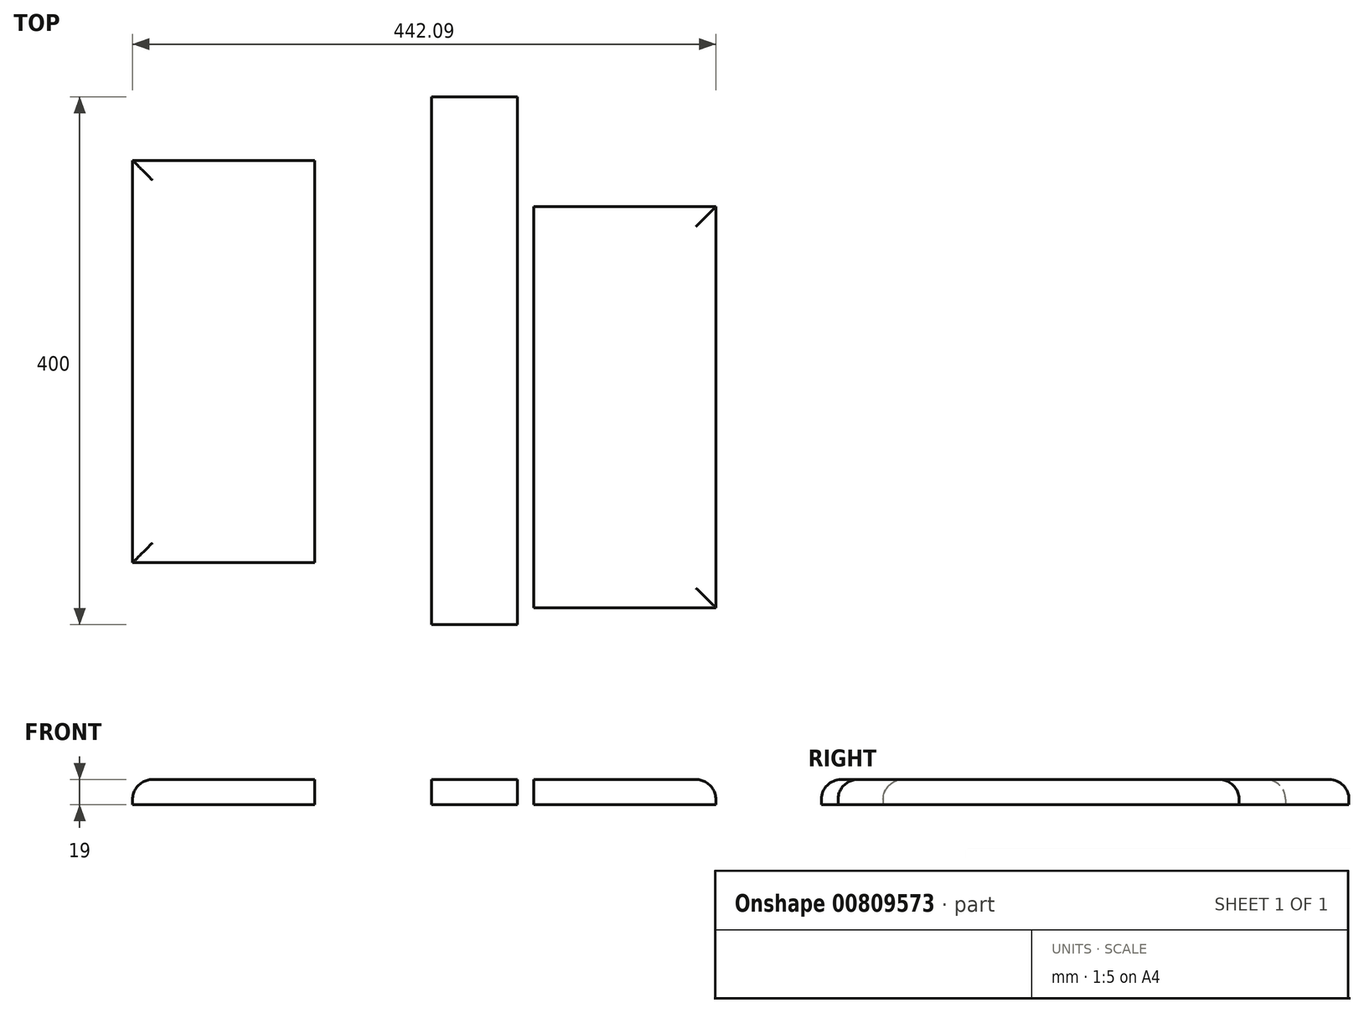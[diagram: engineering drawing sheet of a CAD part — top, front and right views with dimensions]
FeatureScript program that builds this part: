
annotation { "Feature Type Name" : "Feature", "Feature Type Description" : "" }
export const myFeature = defineFeature(function(context is Context, id is Id, definition is map)
    precondition{}
    {
        {
            var Q0;
            Q0=qCreatedBy(makeId("Top.planeOp"),FACE);
            var sketch = newSketch(context, id + "F0", { "sketchPlane" : qUnion([Q0])});
            skLineSegment(sketch, "E0.bottom", {"start": v(-51.89, 169.58) * mm, "end": v(-116.89, 169.58) * mm});
            skLineSegment(sketch, "E0.top", {"start": v(-51.89, -230.42) * mm, "end": v(-116.89, -230.42) * mm});
            skLineSegment(sketch, "E0.left", {"start": v(-51.89, 169.58) * mm, "end": v(-51.89, -230.42) * mm});
            skLineSegment(sketch, "E0.right", {"start": v(-116.89, 169.58) * mm, "end": v(-116.89, -230.42) * mm});
            skSolve(sketch);
        }
        {
            var Q0;
            Q0=makeQuery(id+"F0.imprint","IMPRINT",FACE,{"disambiguationData":[TD([[makeQuery(id+"F0.imprint","IMPRINT",EDGE,{"derivedFrom":sQuery(id+"F0.wireOp",EDGE,"E0.bottom")}),1.0]])]});
            extrude(context, id + "F1", {"entities" : qUnion([Q0]), "depth" : 19 * mm, "offsetDistance" : 25 * mm});
        }
        {
            var Q0;
            Q0=qCreatedBy(makeId("Top.planeOp"),FACE);
            var sketch = newSketch(context, id + "F2", { "sketchPlane" : qUnion([Q0])});
            skLineSegment(sketch, "E1.bottom", {"start": v(-39.45, 86.28) * mm, "end": v(98.55, 86.28) * mm});
            skLineSegment(sketch, "E1.top", {"start": v(-39.45, -217.74) * mm, "end": v(98.55, -217.74) * mm});
            skLineSegment(sketch, "E1.left", {"start": v(-39.45, 86.28) * mm, "end": v(-39.45, -217.74) * mm});
            skLineSegment(sketch, "E1.right", {"start": v(98.55, 86.28) * mm, "end": v(98.55, -217.74) * mm});
            skSolve(sketch);
        }
        {
            var Q0;
            Q0=makeQuery(id+"F2.imprint","IMPRINT",FACE,{"disambiguationData":[TD([[makeQuery(id+"F2.imprint","IMPRINT",EDGE,{"derivedFrom":sQuery(id+"F2.wireOp",EDGE,"E1.bottom")}),-1.0]])]});
            extrude(context, id + "F3", {"entities" : qUnion([Q0]), "depth" : 19 * mm, "offsetDistance" : 25 * mm});
        }
        {
            var Q0;
            Q0=qCreatedBy(makeId("Top.planeOp"),FACE);
            var sketch = newSketch(context, id + "F4", { "sketchPlane" : qUnion([Q0])});
            skLineSegment(sketch, "E2.bottom", {"start": v(-343.54, 121.46) * mm, "end": v(-205.54, 121.46) * mm});
            skLineSegment(sketch, "E2.top", {"start": v(-343.54, -183.54) * mm, "end": v(-205.54, -183.54) * mm});
            skLineSegment(sketch, "E2.left", {"start": v(-343.54, 121.46) * mm, "end": v(-343.54, -183.54) * mm});
            skLineSegment(sketch, "E2.right", {"start": v(-205.54, 121.46) * mm, "end": v(-205.54, -183.54) * mm});
            skSolve(sketch);
        }
        {
            var Q0;
            Q0=makeQuery(id+"F4.imprint","IMPRINT",FACE,{"disambiguationData":[TD([[makeQuery(id+"F4.imprint","IMPRINT",EDGE,{"derivedFrom":sQuery(id+"F4.wireOp",EDGE,"E2.bottom")}),-1.0]])]});
            extrude(context, id + "F5", {"entities" : qUnion([Q0]), "depth" : 19 * mm, "offsetDistance" : 25 * mm});
        }
        {
            var Q0;
            Q0=makeQuery(id+"F1.opExtrude","CAP_EDGE",EDGE,{"disambiguationData":[OSD([sQuery(id+"F0.wireOp",EDGE,"E0.top")])],"isStart":false});
            var Q1;
            Q1=makeQuery(id+"F5.opExtrude","CAP_EDGE",EDGE,{"disambiguationData":[OSD([sQuery(id+"F4.wireOp",EDGE,"E2.top")])],"isStart":false});
            var Q2;
            Q2=makeQuery(id+"F5.opExtrude","CAP_EDGE",EDGE,{"disambiguationData":[OSD([sQuery(id+"F4.wireOp",EDGE,"E2.left")])],"isStart":false});
            var Q3;
            Q3=makeQuery(id+"F5.opExtrude","CAP_EDGE",EDGE,{"disambiguationData":[OSD([sQuery(id+"F4.wireOp",EDGE,"E2.bottom")])],"isStart":false});
            var Q4;
            Q4=makeQuery(id+"F1.opExtrude","CAP_EDGE",EDGE,{"disambiguationData":[OSD([sQuery(id+"F0.wireOp",EDGE,"E0.bottom")])],"isStart":false});
            var Q5;
            Q5=makeQuery(id+"F3.opExtrude","CAP_EDGE",EDGE,{"disambiguationData":[OSD([sQuery(id+"F2.wireOp",EDGE,"E1.bottom")])],"isStart":false});
            var Q6;
            Q6=makeQuery(id+"F3.opExtrude","CAP_EDGE",EDGE,{"disambiguationData":[OSD([sQuery(id+"F2.wireOp",EDGE,"E1.right")])],"isStart":false});
            var Q7;
            Q7=makeQuery(id+"F3.opExtrude","CAP_EDGE",EDGE,{"disambiguationData":[OSD([sQuery(id+"F2.wireOp",EDGE,"E1.top")])],"isStart":false});
            fillet(context, id + "F6", {"entities" : qUnion([Q0, Q1, Q2, Q3, Q4, Q5, Q6, Q7]), "radius" : 15 * mm, "tangentPropagation" : true, "allowEdgeOverflow" : false});
        }
    });
